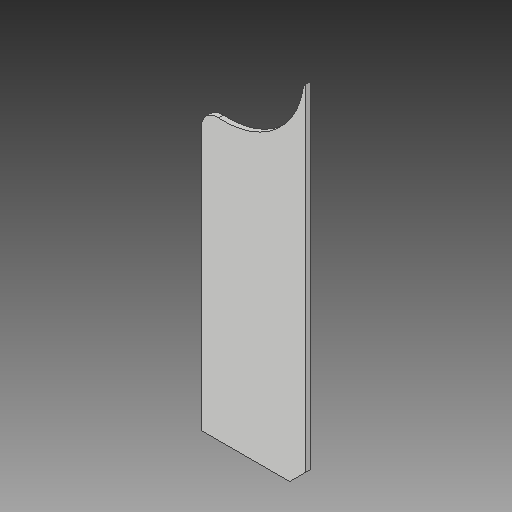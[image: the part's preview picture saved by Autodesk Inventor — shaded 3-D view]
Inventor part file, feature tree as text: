
AUTODESK INVENTOR PART (.ipt)
format: ipt  version: 2017 (Build 210142000, 142)  size: 110,080 bytes
history: native  units: in
note: dims shown in document units (in); Inventor stores cm internally (conversion verified against a paired STEP export)
features: hole x2, fillet x2, extrude x1, chamfer x1, sketch x1
ambient origin geometry x8: Origin, YZ Plane, XZ Plane, XY Plane, X Axis, Y Axis, Z Axis, Center Point
bodies: Solid1 (feature_tree)
feature tree (7):
  extrude  "Extrusion1"  Depth=12.0in
  chamfer  "Chamfer1"  Distance=0.15in
  hole  "Hole1"  [1 undecoded]
  hole  "Hole2"  [1 undecoded]
  fillet  "Fillet1"  Radius=0.3in
  fillet  "Fillet2"  Radius=0.5in
  sketch  "Sketch1"  dims[d0=3.25in d1=12.0in d2=0.15in d3=0.0in d4=0.5in d5=0.125in d6=45.0deg d7=0.8in d8=0.7in d9=5.0in d10=0.75in d11=0.375in d12=0.25in d13=0.5635in d14=1.0in d15=0.8108in d16=1.0in d17=1.0in d18=1.9in d19=0.75in d20=0.375in d21=0.25in d22=0.5635in d23=1.0in d24=0.8108in d25=0.3in d26=0.5in]
note: 2 required parameter values undecoded (feature->parameter linkage not recoverable at this tier; creation-order binding heuristic only, values carry confidence <= 0.55)
